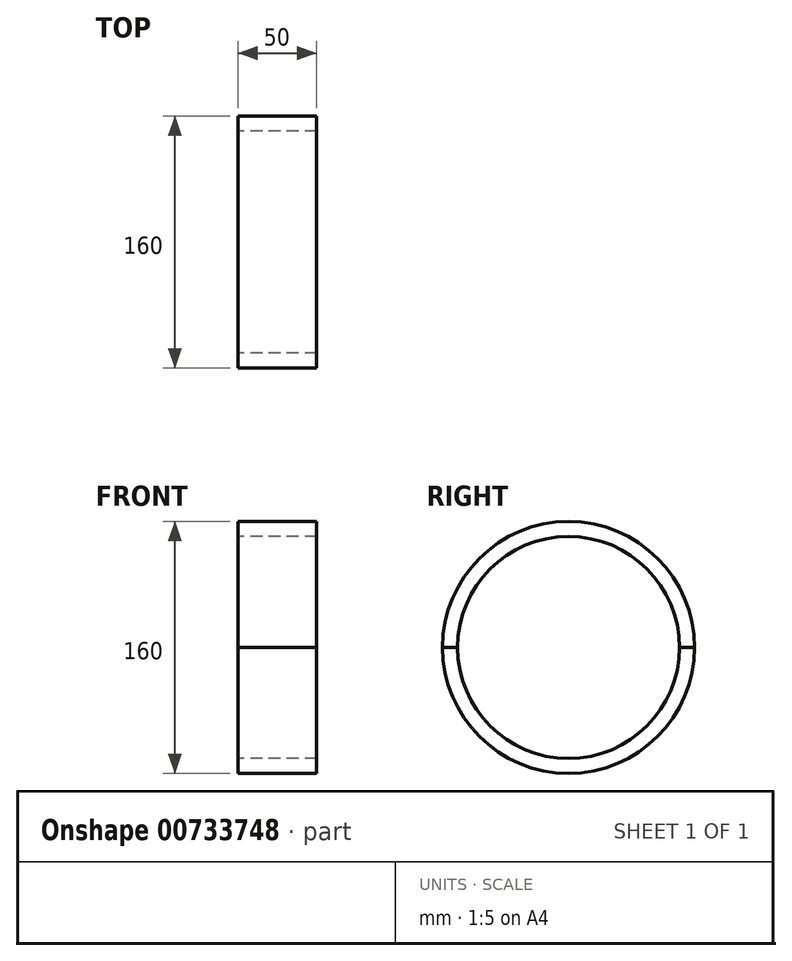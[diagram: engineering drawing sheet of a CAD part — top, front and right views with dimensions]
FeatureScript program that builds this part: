
annotation { "Feature Type Name" : "Feature", "Feature Type Description" : "" }
export const myFeature = defineFeature(function(context is Context, id is Id, definition is map)
    precondition{}
    {
        {
            var Q0;
            Q0=qCreatedBy(makeId("Front.planeOp"),FACE);
            var sketch = newSketch(context, id + "F0", { "sketchPlane" : qUnion([Q0])});
            skLineSegment(sketch, "E0.bottom", {"start": v(25, -80) * mm, "end": v(-25, -80) * mm});
            skLineSegment(sketch, "E0.top", {"start": v(25, 80) * mm, "end": v(-25, 80) * mm});
            skLineSegment(sketch, "E0.left", {"start": v(25, -80) * mm, "end": v(25, 80) * mm});
            skLineSegment(sketch, "E0.right", {"start": v(-25, -80) * mm, "end": v(-25, 80) * mm});
            skPoint(sketch, "E0.middle", {"position": v(0, 0) * mm});
            skLineSegment(sketch, "E1.bottom", {"start": v(25, -70.5) * mm, "end": v(-25, -70.5) * mm});
            skLineSegment(sketch, "E1.top", {"start": v(25, 70.5) * mm, "end": v(-25, 70.5) * mm});
            skLineSegment(sketch, "E1.left", {"start": v(25, -70.5) * mm, "end": v(25, 70.5) * mm});
            skLineSegment(sketch, "E1.right", {"start": v(-25, -70.5) * mm, "end": v(-25, 70.5) * mm});
            skLineSegment(sketch, "E2", {"start": v(0, 0) * mm, "end": v(200, 0) * mm, "construction": true});
            skSolve(sketch);
        }
        {
            var Q0;
            {var subQ0=sQuery(id+"F0.wireOp",EDGE,"E0.top");Q0=makeQuery(id+"F0.imprint","IMPRINT",FACE,{"disambiguationData":[TD([[makeQuery(id+"F0.imprint","IMPRINT",EDGE,{"derivedFrom":subQ0}),1.0]])]});}
            var Q1;
            {var subQ0=sQuery(id+"F0.wireOp",EDGE,"E0.bottom");Q1=makeQuery(id+"F0.imprint","IMPRINT",FACE,{"disambiguationData":[TD([[makeQuery(id+"F0.imprint","IMPRINT",EDGE,{"derivedFrom":subQ0}),-1.0]])]});}
            var Q2;
            Q2=sQuery(id+"F0.wireOp",EDGE,"E2");
            revolve(context, id + "F1", {"surfaceOperationType" : NewSurfaceOperationType.NEW, "entities" : qUnion([Q0, Q1]), "axis" : qUnion([Q2]), "revolveType" : RevolveType.SYMMETRIC, "angle" : 180 * degree});
        }
    });
